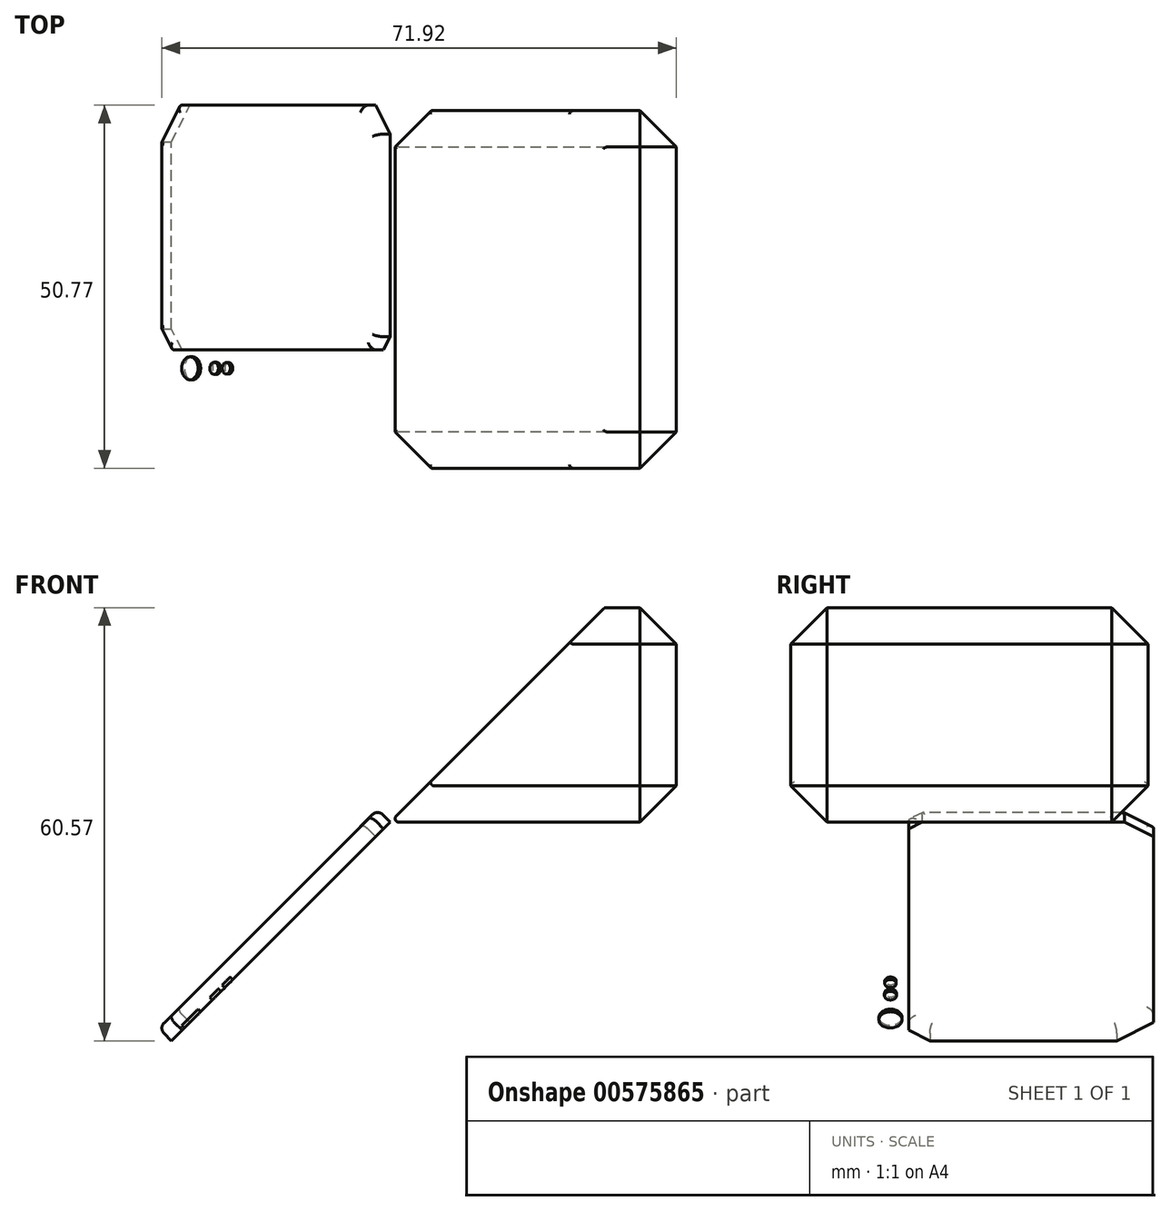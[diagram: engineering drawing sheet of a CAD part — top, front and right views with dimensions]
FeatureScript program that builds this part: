
annotation { "Feature Type Name" : "Feature", "Feature Type Description" : "" }
export const myFeature = defineFeature(function(context is Context, id is Id, definition is map)
    precondition{}
    {
        {
            var Q0;
            Q0=qCreatedBy(makeId("Front.planeOp"),FACE);
            var sketch = newSketch(context, id + "F0", { "sketchPlane" : qUnion([Q0])});
            skLineSegment(sketch, "E0", {"start": v(-26.38, 21.05) * mm, "end": v(3.62, 51.05) * mm});
            skLineSegment(sketch, "E1", {"start": v(3.62, 51.05) * mm, "end": v(13.62, 51.05) * mm});
            skLineSegment(sketch, "E2", {"start": v(13.62, 51.05) * mm, "end": v(13.62, 21.05) * mm});
            skLineSegment(sketch, "E3", {"start": v(13.62, 21.05) * mm, "end": v(-26.38, 21.05) * mm});
            skSolve(sketch);
        }
        {
            var Q0;
            Q0 = qSketchRegion(id + "F0", true);
            extrude(context, id + "F1", {"entities" : qUnion([Q0]), "depth" : 50 * mm, "offsetDistance" : 25.4 * mm});
        }
        {
            var Q0;
            Q0=makeQuery(id+"F1.opExtrude","SWEPT_FACE",FACE,{"disambiguationData":[OSD([sQuery(id+"F0.wireOp",EDGE,"E0")])]});
            var sketch = newSketch(context, id + "F2", { "sketchPlane" : qUnion([Q0])});
            skLineSegment(sketch, "E4", {"start": v(33.46, -44.92) * mm, "end": v(30.52, -47) * mm});
            skLineSegment(sketch, "E5", {"start": v(30.52, -47) * mm, "end": v(4.37, -47) * mm});
            skLineSegment(sketch, "E6", {"start": v(4.37, -47) * mm, "end": v(-0.77, -43.37) * mm});
            skLineSegment(sketch, "E7", {"start": v(-0.77, -43.37) * mm, "end": v(-0.77, -6.63) * mm});
            skLineSegment(sketch, "E8", {"start": v(-0.77, -6.63) * mm, "end": v(4.37, -3) * mm});
            skLineSegment(sketch, "E9", {"start": v(4.37, -3) * mm, "end": v(30.52, -3) * mm});
            skLineSegment(sketch, "E10", {"start": v(30.52, -3) * mm, "end": v(33.46, -5.08) * mm});
            skLineSegment(sketch, "E11", {"start": v(33.46, -5.08) * mm, "end": v(33.46, -44.92) * mm});
            skSolve(sketch);
        }
        {
            var Q0;
            Q0=makeQuery(id+"F2.imprint","IMPRINT",FACE,{"disambiguationData":[TD([[makeQuery(id+"F2.imprint","IMPRINT",EDGE,{"derivedFrom":sQuery(id+"F2.wireOp",EDGE,"E4")}),-1.0]])]});
            extrude(context, id + "F3", {"entities" : qUnion([Q0]), "operationType" : NewBodyOperationType.ADD, "depth" : 2.5 * mm, "offsetDistance" : 25.4 * mm});
        }
        {
            var Q0;
            Q0=makeQuery(id+"F3.opExtrude","CAP_EDGE",EDGE,{"disambiguationData":[OSD([sQuery(id+"F2.wireOp",EDGE,"E9")])],"isStart":false});
            var Q1;
            Q1=makeQuery(id+"F3.opExtrude","CAP_FACE",FACE,{"disambiguationData":[OSD([sQuery(id+"F2.wireOp",EDGE,"E4"),sQuery(id+"F2.wireOp",EDGE,"E5"),sQuery(id+"F2.wireOp",EDGE,"E6"),sQuery(id+"F2.wireOp",EDGE,"E7"),sQuery(id+"F2.wireOp",EDGE,"E8"),sQuery(id+"F2.wireOp",EDGE,"E9"),sQuery(id+"F2.wireOp",EDGE,"E10"),sQuery(id+"F2.wireOp",EDGE,"E11")])],"isStart":false});
            fillet(context, id + "F4", {"entities" : qUnion([Q0, Q1]), "radius" : 1 * mm, "tangentPropagation" : true, "allowEdgeOverflow" : false});
        }
        {
            var Q0;
            Q0=makeQuery(id+"F1.opExtrude","SWEPT_FACE",FACE,{"disambiguationData":[OSD([sQuery(id+"F0.wireOp",EDGE,"E0")])]});
            var sketch = newSketch(context, id + "F5", { "sketchPlane" : qUnion([Q0])});
            skCircle(sketch, "E12", {"center": v(36.03, -42.86) * mm, "radius": 1.62 * mm});
            skCircle(sketch, "E13", {"center": v(36.03, -38.08) * mm, "radius": 0.84 * mm});
            skCircle(sketch, "E14", {"center": v(36.03, -35.69) * mm, "radius": 0.8 * mm});
            skSolve(sketch);
        }
        {
            var Q0;
            Q0 = qSketchRegion(id + "F5", true);
            extrude(context, id + "F6", {"entities" : qUnion([Q0]), "operationType" : NewBodyOperationType.ADD, "depth" : 0.5 * mm, "offsetDistance" : 25.4 * mm});
        }
        {
            var Q0;
            Q0=makeQuery(id+"F1.opExtrude","CAP_EDGE",EDGE,{"disambiguationData":[OSD([sQuery(id+"F0.wireOp",EDGE,"E3")])],"isStart":true});
            var Q1;
            Q1=makeQuery(id+"F1.opExtrude","CAP_EDGE",EDGE,{"disambiguationData":[OSD([sQuery(id+"F0.wireOp",EDGE,"E3")])],"isStart":false});
            var Q2;
            Q2=makeQuery(id+"F1.opExtrude","CAP_EDGE",EDGE,{"disambiguationData":[OSD([sQuery(id+"F0.wireOp",EDGE,"E1")])],"isStart":false});
            var Q3;
            Q3=makeQuery(id+"F1.opExtrude","CAP_EDGE",EDGE,{"disambiguationData":[OSD([sQuery(id+"F0.wireOp",EDGE,"E2")])],"isStart":false});
            var Q4;
            Q4=makeQuery(id+"F1.opExtrude","SWEPT_EDGE",EDGE,{"disambiguationData":[OSD([sQuery(id+"F0.wireOp",EDGE,"E1"),sQuery(id+"F0.wireOp",EDGE,"E2")])]});
            var Q5;
            Q5=makeQuery(id+"F1.opExtrude","CAP_EDGE",EDGE,{"disambiguationData":[OSD([sQuery(id+"F0.wireOp",EDGE,"E1")])],"isStart":true});
            var Q6;
            Q6=makeQuery(id+"F1.opExtrude","CAP_EDGE",EDGE,{"disambiguationData":[OSD([sQuery(id+"F0.wireOp",EDGE,"E2")])],"isStart":true});
            var Q7;
            Q7=makeQuery(id+"F1.opExtrude","SWEPT_EDGE",EDGE,{"disambiguationData":[OSD([sQuery(id+"F0.wireOp",EDGE,"E2"),sQuery(id+"F0.wireOp",EDGE,"E3")])]});
            chamfer(context, id + "F7", {"entities" : qUnion([Q0, Q1, Q2, Q3, Q4, Q5, Q6, Q7]), "width" : 5.08 * mm, "tangentPropagation" : true});
        }
        {
            var Q0;
            Q0=makeQuery(id+"F1.opExtrude","SWEPT_EDGE",EDGE,{"disambiguationData":[OSD([sQuery(id+"F0.wireOp",EDGE,"E0"),sQuery(id+"F0.wireOp",EDGE,"E3")])]});
            var Q1;
            Q1=makeQuery(id+"F7.opChamfer","BLEND_EDGE",EDGE,{"blendedFrom":[makeQuery(id+"F1.opExtrude","CAP_EDGE",EDGE,{"disambiguationData":[OSD([sQuery(id+"F0.wireOp",EDGE,"E3")])],"isStart":true}),makeQuery(id+"F1.opExtrude","SWEPT_FACE",FACE,{"disambiguationData":[OSD([sQuery(id+"F0.wireOp",EDGE,"E0")])]})],"blendedInto":[makeQuery(id+"F1.opExtrude","SWEPT_FACE",FACE,{"disambiguationData":[OSD([sQuery(id+"F0.wireOp",EDGE,"E0")])]})]});
            var Q2;
            Q2=makeQuery(id+"F1.opExtrude","CAP_EDGE",EDGE,{"disambiguationData":[OSD([sQuery(id+"F0.wireOp",EDGE,"E0")])],"isStart":true});
            var Q3;
            Q3=makeQuery(id+"F7.opChamfer","BLEND_EDGE",EDGE,{"blendedFrom":[makeQuery(id+"F1.opExtrude","CAP_EDGE",EDGE,{"disambiguationData":[OSD([sQuery(id+"F0.wireOp",EDGE,"E3")])],"isStart":false}),makeQuery(id+"F1.opExtrude","SWEPT_FACE",FACE,{"disambiguationData":[OSD([sQuery(id+"F0.wireOp",EDGE,"E0")])]})],"blendedInto":[makeQuery(id+"F1.opExtrude","SWEPT_FACE",FACE,{"disambiguationData":[OSD([sQuery(id+"F0.wireOp",EDGE,"E0")])]})]});
            var Q4;
            Q4=makeQuery(id+"F1.opExtrude","CAP_EDGE",EDGE,{"disambiguationData":[OSD([sQuery(id+"F0.wireOp",EDGE,"E0")])],"isStart":false});
            var Q5;
            Q5=makeQuery(id+"F7.opChamfer","BLEND_EDGE",EDGE,{"blendedFrom":[makeQuery(id+"F1.opExtrude","CAP_EDGE",EDGE,{"disambiguationData":[OSD([sQuery(id+"F0.wireOp",EDGE,"E1")])],"isStart":false}),makeQuery(id+"F1.opExtrude","SWEPT_FACE",FACE,{"disambiguationData":[OSD([sQuery(id+"F0.wireOp",EDGE,"E0")])]})],"blendedInto":[makeQuery(id+"F1.opExtrude","SWEPT_FACE",FACE,{"disambiguationData":[OSD([sQuery(id+"F0.wireOp",EDGE,"E0")])]})]});
            var Q6;
            Q6=makeQuery(id+"F1.opExtrude","SWEPT_EDGE",EDGE,{"disambiguationData":[OSD([sQuery(id+"F0.wireOp",EDGE,"E0"),sQuery(id+"F0.wireOp",EDGE,"E1")])]});
            var Q7;
            Q7=makeQuery(id+"F7.opChamfer","BLEND_EDGE",EDGE,{"blendedFrom":[makeQuery(id+"F1.opExtrude","CAP_EDGE",EDGE,{"disambiguationData":[OSD([sQuery(id+"F0.wireOp",EDGE,"E1")])],"isStart":true}),makeQuery(id+"F1.opExtrude","SWEPT_FACE",FACE,{"disambiguationData":[OSD([sQuery(id+"F0.wireOp",EDGE,"E0")])]})],"blendedInto":[makeQuery(id+"F1.opExtrude","SWEPT_FACE",FACE,{"disambiguationData":[OSD([sQuery(id+"F0.wireOp",EDGE,"E0")])]})]});
            fillet(context, id + "F8", {"entities" : qUnion([Q0, Q1, Q2, Q3, Q4, Q5, Q6, Q7]), "radius" : 0.5 * mm, "tangentPropagation" : true, "allowEdgeOverflow" : false});
        }
    });
